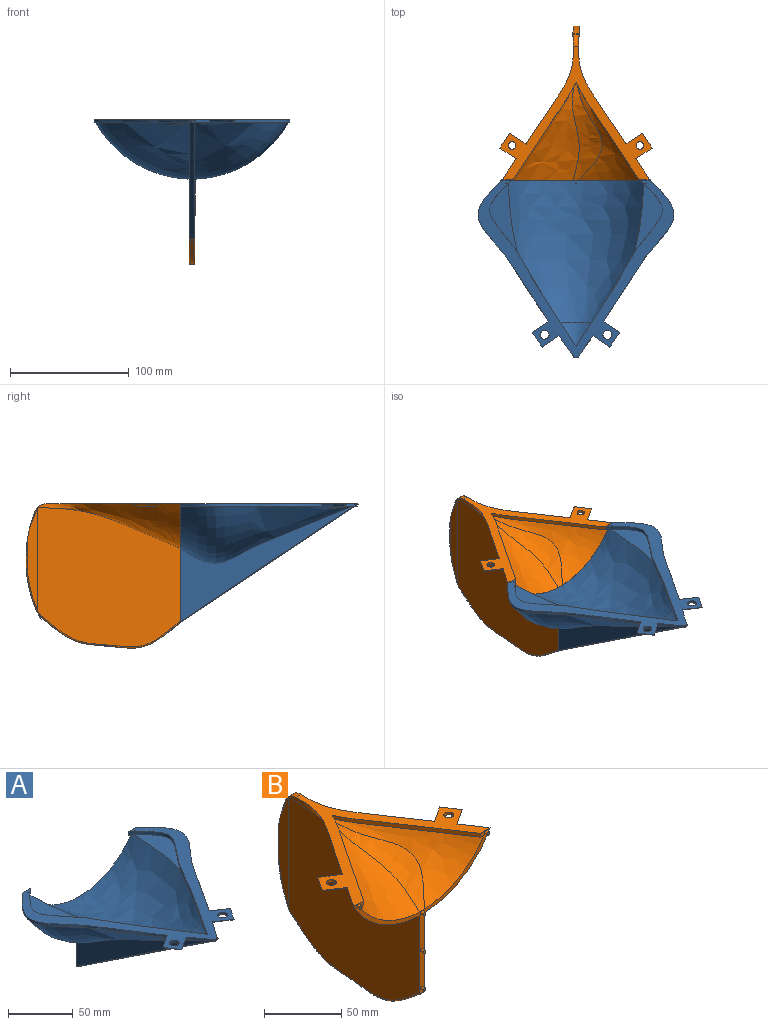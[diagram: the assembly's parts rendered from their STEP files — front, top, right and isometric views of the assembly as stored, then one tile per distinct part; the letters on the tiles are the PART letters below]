
ASSEMBLY  parts=2 mates=1
PART A: 59 faces, bbox 246.2x251.8x187.3 mm
  f0: plane 224.77x209.27mm, normal (0,0,-1), area 377.1mm2, adj f4,f5,f6,f7,f8,f9,f10,f16
  f1: plane 2.46x1.47mm, normal (0,0,-1), area 1.2mm2, adj f41,f54,f55
  f2: plane 2.46x1.47mm, normal (0,0,-1), area 1.2mm2, adj f41,f53,f54
  f3: plane 2.46x1.47mm, normal (0,0,-1), area 1.2mm2, adj f40,f57,f58
  f4: bspline ~150x92.38mm, area 5890.7mm2, adj f0,f8,f16
  f5: bspline ~150x92.38mm, area 5890.7mm2, adj f0,f6,f16
  f6: plane 146.81x97.54mm, normal (1,0,0), area 3010.2mm2, adj f0,f5,f9,f16
  f7: bspline ~150x99.5mm, area 707.8mm2, adj f0,f9,f10,f16
  f8: bspline ~150x100mm, area 3031.6mm2, adj f0,f4,f10,f16
  f9: bspline ~180.9x120.3mm, area 138.6mm2, adj f0,f6,f7,f16
  f10: bspline ~164.39x109.36mm, area 138.5mm2, adj f0,f7,f8,f16
  f11: plane 3.63x2.9mm, normal (0,0,1), area 0.5mm2, adj f26,f27,f34
  f12: plane 165.03x149.59mm, normal (0,0,1), area 3197.7mm2, adj f16,f17,f18,f26,f27,f28,f35,f37
  f13: plane 78.2x48.71mm, normal (0,0,-1), area 235.7mm2, adj f23,f26,f34
  f14: plane 4.21x3.81mm, normal (0,0,-1), area 6.2mm2, adj f16,f23,f26
  f15: plane 78.06x48.57mm, normal (0,0,-1), area 223mm2, adj f23,f27,f34
  f16: plane 125.9x100.9mm, normal (0,1,0), area 759.4mm2, adj f0,f4,f5,f6,f7,f8,f9,f10
  f17: bspline ~59.99x42.31mm, area 2.2mm2, adj f12,f21,f28,f31,f35
  f18: bspline ~59.99x42.31mm, area 2.3mm2, adj f12,f19,f28,f29,f37
  f19: plane 1.78x1.16mm, normal (1,0,0), area 0.4mm2, adj f18,f29,f30,f37
  f20: bspline ~59.99x39.53mm, area 2.3mm2, adj f30,f32,f33,f35,f36,f37
  f21: bspline ~59.99x40.03mm, area 0.4mm2, adj f17,f31,f33,f35
  f22: plane 4.21x3.73mm, normal (0,0,-1), area 6.2mm2, adj f16,f23,f27
  f23: bspline ~120x114.56mm, area 13093.4mm2, adj f13,f14,f15,f16,f22,f24,f25,f34
  f24: plane 57.76x23.61mm, normal (0,0,1), area 564.9mm2, adj f23,f27
  f25: plane 57.76x23.61mm, normal (0,0,1), area 559.9mm2, adj f23,f26
  f26: extruded ~140.36x72.66mm, area 507.3mm2, adj f11,f12,f13,f14,f16,f25,f27
  f27: extruded ~140.36x72.66mm, area 507.3mm2, adj f11,f12,f15,f16,f22,f24,f26
  f28: cylinder r=0.5mm len=2.4mm, axis (1,0,0), area 1.5mm2, adj f12,f17,f18,f29,f31,f32
  f29: bspline ~1.72x0.78mm, area 0.8mm2, adj f18,f19,f28,f30,f32
  f30: bspline ~25.49x16.71mm, area 1.7mm2, adj f19,f20,f29,f32,f37
  f31: bspline ~1.72x0.78mm, area 0.8mm2, adj f17,f21,f28,f32,f33
  f32: bspline ~6.46x0.42mm, area 1.4mm2, adj f20,f28,f29,f30,f31,f33
  f33: bspline ~4.82x3.36mm, area 1.7mm2, adj f20,f21,f31,f32,f35
  f34: bspline ~32.45x20mm, area 386.1mm2, adj f11,f13,f15,f23
  f35: extruded ~21.5x15.61mm, area 48.1mm2, adj f0,f12,f17,f20,f21,f33,f36,f58
  f36: plane 2.4x1.34mm, normal (0,-1,0), area 3.2mm2, adj f0,f20,f35,f37
  f37: extruded ~21.5x15.61mm, area 47.1mm2, adj f0,f12,f18,f19,f20,f30,f36,f53
  f38: extruded ~122.49x61.71mm, area 313.9mm2, adj f0,f12,f16,f55
  f39: extruded ~122.49x61.71mm, area 317.7mm2, adj f0,f12,f16,f56
  f40: cylinder r=3.75mm len=7.5mm, axis (0,0,1), area 50.9mm2, adj f0,f3,f12,f42,f56,f57,f58
  f41: cylinder r=3.75mm len=7.5mm, axis (0,0,1), area 50.9mm2, adj f0,f1,f2,f12,f53,f54,f55
  f42: plane 2.46x1.47mm, normal (0,0,-1), area 1.2mm2, adj f40,f56,f57
  f43: cylinder r=1.35mm len=2.7mm, axis (0,1,0), area 22.9mm2, adj f16,f44
  f44: plane 2.7x2.7mm, normal (0,1,0), area 5.7mm2, adj f43
  f45: cylinder r=1.35mm len=2.7mm, axis (0,1,0), area 22.9mm2, adj f16,f46
  f46: plane 2.7x2.7mm, normal (0,1,0), area 5.7mm2, adj f45
  f47: cylinder r=1.35mm len=2.7mm, axis (0,1,0), area 22.9mm2, adj f16,f48
  f48: plane 2.7x2.7mm, normal (0,1,0), area 5.7mm2, adj f47
  f49: cylinder r=1.35mm len=2.7mm, axis (0,1,0), area 22.9mm2, adj f16,f50
  f50: plane 2.7x2.7mm, normal (0,1,0), area 5.7mm2, adj f49
  f51: cylinder r=1.35mm len=2.7mm, axis (0,1,0), area 22.9mm2, adj f16,f52
  f52: plane 2.7x2.7mm, normal (0,1,0), area 5.7mm2, adj f51
  f53: cylinder r=5mm len=16.38mm, axis (0.83,-0.56,0), area 71.1mm2, adj f0,f2,f12,f37,f41,f54
  f54: cylinder r=5mm len=14.74mm, axis (0.56,0.83,0), area 51.8mm2, adj f1,f2,f12,f41,f53,f55
  f55: cylinder r=5mm len=16.13mm, axis (-0.83,0.56,0), area 69.7mm2, adj f0,f1,f12,f38,f41,f54
  f56: cylinder r=5mm len=16.13mm, axis (0.83,0.56,0), area 69.7mm2, adj f0,f12,f39,f40,f42,f57
  f57: cylinder r=5mm len=14.74mm, axis (-0.56,0.83,0), area 51.8mm2, adj f3,f12,f40,f42,f56,f58
  f58: cylinder r=5mm len=16.38mm, axis (-0.83,-0.56,0), area 71.1mm2, adj f0,f3,f12,f35,f40,f57
PART B: 55 faces, bbox 128.6x140.2x126.9 mm
  f0: bspline ~120x61.4mm, area 3792.9mm2, adj f3,f4,f6,f14,f19,f46,f52,f54
  f1: bspline ~71.93x29.55mm, area 3.8mm2, adj f15,f17,f33
  f2: bspline ~71.93x29.55mm, area 0mm2, adj f6,f15,f33
  f3: plane 125.32x100.32mm, normal (0,-1,0), area 760.8mm2, adj f0,f4,f5,f6,f7,f8,f9,f22
  f4: plane 128.3x113.19mm, normal (0,0,1), area 2138.9mm2, adj f0,f3,f9,f19,f25,f26,f45,f47
  f5: bspline ~114.56x90mm, area 615.3mm2, adj f3,f21,f22,f24,f25,f26
  f6: bspline ~122.27x120mm, area 11691.5mm2, adj f0,f2,f3,f15,f33,f34
  f7: bspline ~120x32.27mm, area 396.3mm2, adj f3,f20,f27,f34
  f8: bspline ~122.27x120mm, area 11691.2mm2, adj f3,f9,f11,f27,f28,f29
  f9: bspline ~120x61.4mm, area 3793.7mm2, adj f3,f4,f8,f12,f19,f48,f49,f51
  f10: plane 4.06x3.82mm, normal (0,1,0), area 15.5mm2, adj f15,f17,f18,f31
  f11: plane 87.47x9.18mm, normal (-1,0,0), area 557.1mm2, adj f8,f12,f18,f29,f30,f31
  f12: bspline ~20.31x6.92mm, area 11.8mm2, adj f9,f11,f13,f18,f19
  f13: plane 5.1x3.67mm, normal (0,0.94,0.35), area 19.9mm2, adj f12,f14,f18,f19
  f14: bspline ~28x10mm, area 11.8mm2, adj f0,f13,f15,f18,f19
  f15: plane 94.52x12.73mm, normal (1,-0.01,0), area 615.4mm2, adj f1,f2,f6,f10,f14,f17,f18
  f16: plane 4.92x3mm, normal (0,0.93,-0.37), area 15.9mm2, adj f17,f20,f29,f32
  f17: cylinder r=100mm len=48.71mm, axis (-1,0,0), area 159.2mm2, adj f1,f10,f15,f16,f30,f32
  f18: cylinder r=100mm len=34.73mm, axis (-1,0,0), area 172.4mm2, adj f10,f11,f12,f13,f14,f15,f31
  f19: cylinder r=10mm len=9.38mm, axis (-1,0,0), area 59.3mm2, adj f0,f4,f9,f12,f13,f14
  f20: bspline ~4.73x3.78mm, area 14mm2, adj f7,f16,f28,f33
  f21: plane 1.91x1.91mm, normal (0,-1,0), area 1.8mm2, adj f5,f22,f24
  f22: bspline ~90x57.28mm, area 2021.8mm2, adj f3,f5,f21,f23
  f23: bspline ~90x30.05mm, area 1143.7mm2, adj f3,f22,f24
  f24: bspline ~90x63.2mm, area 3107.1mm2, adj f3,f5,f21,f23
  f25: extruded ~82.27x53.47mm, area 277.8mm2, adj f3,f4,f5,f26
  f26: extruded ~82.27x53.47mm, area 279.8mm2, adj f3,f4,f5,f25
  f27: bspline ~128x32.34mm, area 207.3mm2, adj f3,f7,f8,f28
  f28: bspline ~5.82x4.65mm, area 7.1mm2, adj f8,f20,f27,f29
  f29: bspline ~71.93x29.55mm, area 8.3mm2, adj f8,f11,f16,f28,f30
  f30: bspline ~54.25x12.8mm, area 58.9mm2, adj f11,f17,f29,f31
  f31: bspline ~48.17x1mm, area 16.7mm2, adj f10,f11,f18,f30
  f32: bspline ~71.93x29.55mm, area 1.4mm2, adj f16,f17,f33
  f33: bspline ~5.82x4.65mm, area 7.1mm2, adj f1,f2,f6,f20,f32,f34
  f34: bspline ~123.77x29.02mm, area 207.3mm2, adj f3,f6,f7,f33
  f35: cylinder r=1.25mm len=2.5mm, axis (0,1,0), area 19.6mm2, adj f3,f36
  f36: plane 2.5x2.5mm, normal (0,-1,0), area 4.9mm2, adj f35
  f37: cylinder r=1.25mm len=2.5mm, axis (0,1,0), area 19.6mm2, adj f3,f38
  f38: plane 2.5x2.5mm, normal (0,-1,0), area 4.9mm2, adj f37
  f39: cylinder r=1.25mm len=2.5mm, axis (0,1,0), area 19.6mm2, adj f3,f40
  f40: plane 2.5x2.5mm, normal (0,-1,0), area 4.9mm2, adj f39
  f41: cylinder r=1.25mm len=2.5mm, axis (0,1,0), area 19.6mm2, adj f3,f42
  f42: plane 2.5x2.5mm, normal (0,-1,0), area 4.9mm2, adj f41
  f43: cylinder r=1.25mm len=2.5mm, axis (0,1,0), area 19.6mm2, adj f3,f44
  f44: plane 2.5x2.5mm, normal (0,-1,0), area 4.9mm2, adj f43
  f45: cylinder r=3.17mm len=6.35mm, axis (0,0,1), area 43.1mm2, adj f4,f46
  f46: plane 14.98x12.97mm, normal (0,0,-1), area 59.1mm2, adj f0,f45,f52,f53,f54
  f47: cylinder r=3.17mm len=6.35mm, axis (0,0,1), area 43.1mm2, adj f4,f48
  f48: plane 14.98x12.97mm, normal (0,0,-1), area 59.1mm2, adj f9,f47,f49,f50,f51
  f49: cylinder r=5mm len=16.97mm, axis (-0.84,0.54,0), area 72.5mm2, adj f4,f9,f48,f50
  f50: cylinder r=5mm len=14.82mm, axis (-0.54,-0.84,0), area 52.6mm2, adj f4,f48,f49,f51
  f51: cylinder r=5mm len=16.9mm, axis (0.84,-0.54,0), area 71.9mm2, adj f4,f9,f48,f50
  f52: cylinder r=5mm len=16.9mm, axis (-0.84,-0.54,0), area 71.9mm2, adj f0,f4,f46,f53
  f53: cylinder r=5mm len=14.82mm, axis (0.54,-0.84,0), area 52.6mm2, adj f4,f46,f52,f54
  f54: cylinder r=5mm len=16.97mm, axis (0.84,0.54,0), area 72.5mm2, adj f0,f4,f46,f53
PLACE A t=(0.11,-149.82,0.87)mm
PLACE B t=(0.11,-0.02,0.87)mm
MATE fastened B.f37 <-> A.f49  axis (0,-1,0) through (-58.39,-2.52,-0.63)mm
